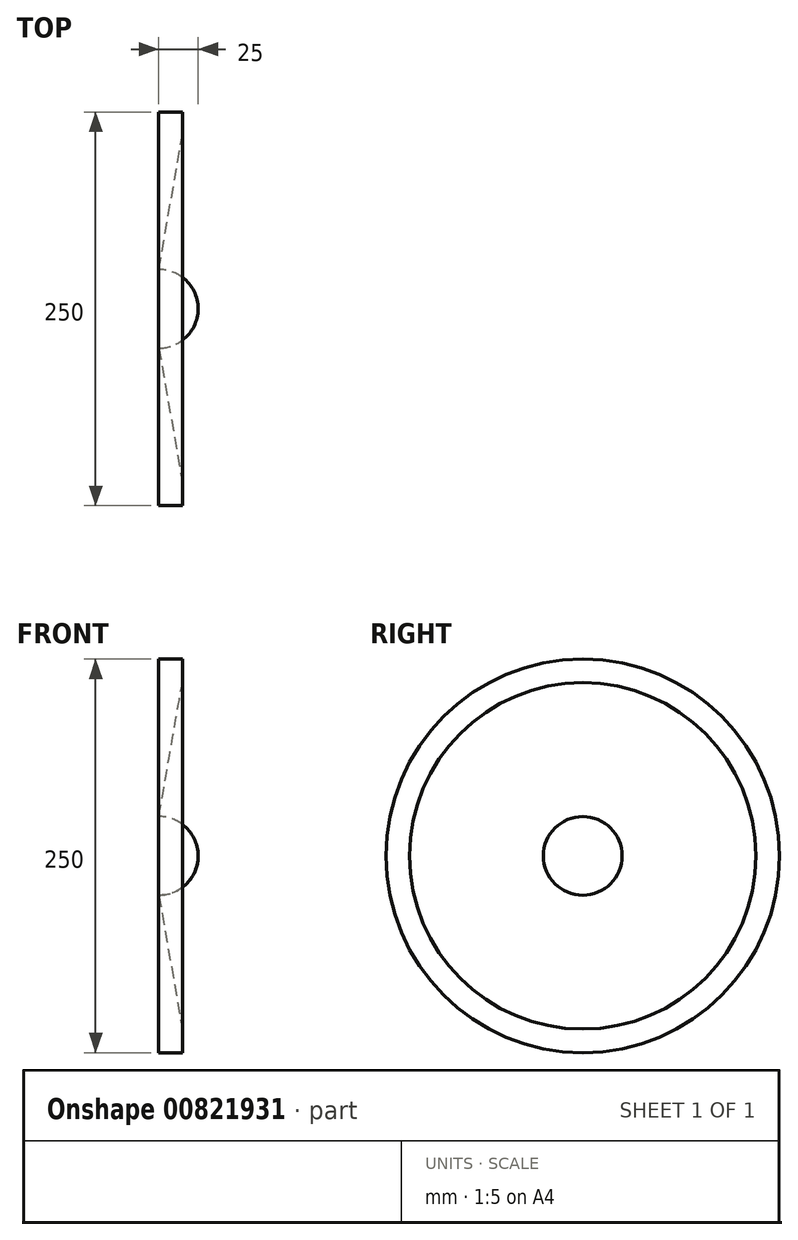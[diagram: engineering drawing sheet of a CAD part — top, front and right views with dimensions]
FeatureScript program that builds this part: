
annotation { "Feature Type Name" : "Feature", "Feature Type Description" : "" }
export const myFeature = defineFeature(function(context is Context, id is Id, definition is map)
    precondition{}
    {
        {
            var Q0;
            Q0=qCreatedBy(makeId("Front.planeOp"),FACE);
            var sketch = newSketch(context, id + "F0", { "sketchPlane" : qUnion([Q0])});
            skLineSegment(sketch, "E0", {"start": v(0, 0) * mm, "end": v(0, 125) * mm});
            skLineSegment(sketch, "E1", {"start": v(0, 125) * mm, "end": v(15, 125) * mm});
            skArc(sketch, "E2", {"start": v(0, 25) * mm, "mid": v(17.68, 17.68) * mm, "end": v(25, 0) * mm});
            skLineSegment(sketch, "E3", {"start": v(0, 0) * mm, "end": v(25, 0) * mm});
            skLineSegment(sketch, "E4", {"start": v(15, 125) * mm, "end": v(15, 110) * mm});
            skLineSegment(sketch, "E5", {"start": v(0, 25) * mm, "end": v(15, 110) * mm});
            skSolve(sketch);
        }
        {
            var Q0;
            Q0 = qSketchRegion(id + "F0", true);
            var Q1;
            Q1=sQuery(id+"F0.wireOp",EDGE,"E3");
            revolve(context, id + "F1", {"surfaceOperationType" : NewSurfaceOperationType.NEW, "entities" : qUnion([Q0]), "axis" : qUnion([Q1]), "revolveType" : RevolveType.FULL});
        }
    });
